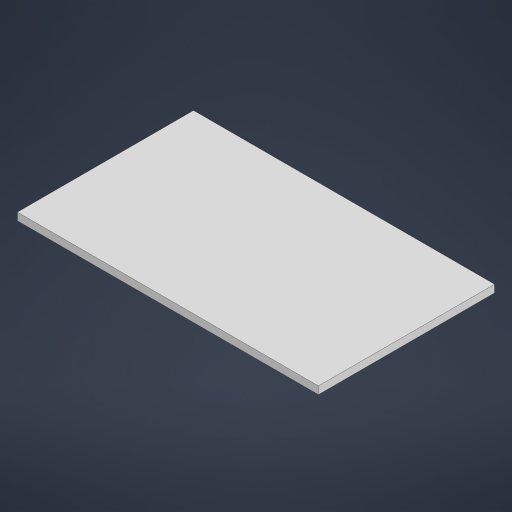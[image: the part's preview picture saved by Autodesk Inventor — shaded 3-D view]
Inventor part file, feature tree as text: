
AUTODESK INVENTOR PART (.ipt)
format: ipt  version: 2023 (Build 270158000, 158)  size: 177,152 bytes
history: native  units: in
note: dims shown in document units (in); Inventor stores cm internally (conversion verified against a paired STEP export)
features: extrude x2, sketch x2, fillet x1
ambient origin geometry x8: Origin, YZ Plane, XZ Plane, XY Plane, X Axis, Y Axis, Z Axis, Center Point
bodies: Solid1 (feature_tree)
feature tree (5):
  extrude  "Extrusion1"  Depth=7.874in
  extrude  "Extrusion2"  Depth=1.5748in
  fillet  "Fillet1"  Radius=0.1969in
  sketch  "Sketch2"  dims[d0=4.6063in d1=7.874in]
  sketch  "Sketch3"  dims[d2=2.3031in d3=3.937in d4=0.1969in d5=0.0in d6=0.2362in d7=0.2362in d8=0.2362in d9=0.2362in d10=0.1575in d11=0.0in d12=1.5748in]
